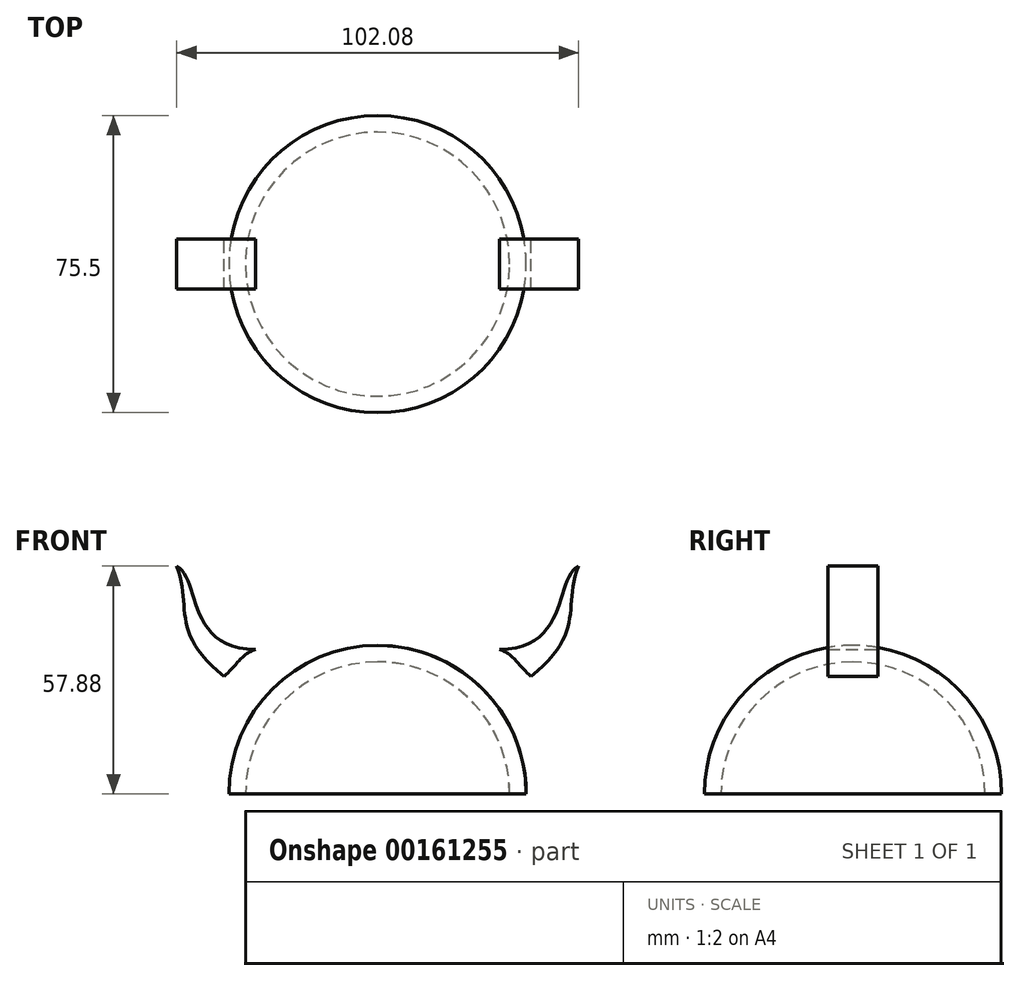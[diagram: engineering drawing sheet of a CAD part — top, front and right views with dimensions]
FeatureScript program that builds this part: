
annotation { "Feature Type Name" : "Feature", "Feature Type Description" : "" }
export const myFeature = defineFeature(function(context is Context, id is Id, definition is map)
    precondition{}
    {
        {
            var Q0;
            Q0=qCreatedBy(makeId("Front.planeOp"),FACE);
            var sketch = newSketch(context, id + "F0", { "sketchPlane" : qUnion([Q0])});
            skArc(sketch, "E0", {"start": v(0, 37.75) * mm, "mid": v(-26.7, 26.7) * mm, "end": v(-37.75, 0) * mm});
            skLineSegment(sketch, "E1", {"start": v(0, 37.75) * mm, "end": v(0, 0) * mm, "construction": true});
            skArc(sketch, "E2", {"start": v(0, 33.57) * mm, "mid": v(-23.74, 23.74) * mm, "end": v(-33.57, 0) * mm});
            skLineSegment(sketch, "E3", {"start": v(-37.75, 0) * mm, "end": v(-33.57, 0) * mm});
            skLineSegment(sketch, "E4", {"start": v(-33.57, 0) * mm, "end": v(0, 0) * mm});
            skLineSegment(sketch, "E5", {"start": v(0, 37.75) * mm, "end": v(0, 33.57) * mm});
            skSolve(sketch);
        }
        {
            var Q0;
            Q0=makeQuery(id+"F0.imprint","IMPRINT",FACE,{"disambiguationData":[TD([[makeQuery(id+"F0.imprint","IMPRINT",EDGE,{"derivedFrom":sQuery(id+"F0.wireOp",EDGE,"E0")}),1.0]])]});
            var Q1;
            Q1=sQuery(id+"F0.wireOp",EDGE,"E1");
            revolve(context, id + "F1", {"entities" : qUnion([Q0]), "axis" : qUnion([Q1]), "revolveType" : RevolveType.FULL});
        }
        {
            var Q0;
            Q0=qCreatedBy(makeId("Front.planeOp"),FACE);
            var sketch = newSketch(context, id + "F2", { "sketchPlane" : qUnion([Q0])});
            skFitSpline(sketch, "E6", {"points": [v(30.95, 36.7) * mm, v(38.96, 29.84) * mm], "startDerivative": vector(10.29, -2.94) * mm, "endDerivative": vector(11.76, -11.27) * mm});
            skFitSpline(sketch, "E7", {"points": [v(30.95, 36.7) * mm, v(51.04, 57.88) * mm], "startDerivative": vector(53.96, 0.83) * mm, "endDerivative": vector(18.25, 8.73) * mm});
            skFitSpline(sketch, "E8", {"points": [v(38.96, 29.84) * mm, v(51.04, 57.88) * mm], "startDerivative": vector(41.9, 33.58) * mm, "endDerivative": vector(12.01, 31.67) * mm});
            skFitSpline(sketch, "E9.MirrorCS", {"points": [v(-38.96, 29.84) * mm, v(-51.04, 57.88) * mm], "startDerivative": vector(-41.9, 33.58) * mm, "endDerivative": vector(-12.01, 31.67) * mm});
            skFitSpline(sketch, "E10.MirrorCS", {"points": [v(-30.95, 36.7) * mm, v(-51.04, 57.88) * mm], "startDerivative": vector(-53.96, 0.83) * mm, "endDerivative": vector(-18.25, 8.73) * mm});
            skFitSpline(sketch, "E11.MirrorCS", {"points": [v(-30.95, 36.7) * mm, v(-38.96, 29.84) * mm], "startDerivative": vector(-10.29, -2.94) * mm, "endDerivative": vector(-11.76, -11.27) * mm});
            skSolve(sketch);
        }
        {
            var Q0;
            Q0 = qSketchRegion(id + "F2", true);
            extrude(context, id + "F3", {"entities" : qUnion([Q0]), "endBound" : BoundingType.SYMMETRIC, "depth" : 12.7 * mm});
        }
        {
            var Q0;
            Q0=qCreatedBy(makeId("Front.planeOp"),FACE);
            var sketch = newSketch(context, id + "F4", { "sketchPlane" : qUnion([Q0])});
            skLineSegment(sketch, "E12", {"start": v(0, 45.84) * mm, "end": v(6.35, 45.84) * mm});
            skLineSegment(sketch, "E13", {"start": v(6.35, 45.84) * mm, "end": v(0, 55.3) * mm});
            skLineSegment(sketch, "E14", {"start": v(0, 55.3) * mm, "end": v(0, 45.84) * mm, "construction": true});
            skSolve(sketch);
        }
        {
            var Q0;
            Q0=sQuery(id+"F4.wireOp",EDGE,"E13");
            var Q1;
            Q1=sQuery(id+"F4.wireOp",EDGE,"E12");
            var Q2;
            Q2=sQuery(id+"F4.wireOp",EDGE,"E14");
            revolve(context, id + "F5", {"bodyType" : ToolBodyType.SURFACE, "surfaceEntities" : qUnion([Q0, Q1]), "axis" : qUnion([Q2]), "revolveType" : RevolveType.FULL});
        }
    });
